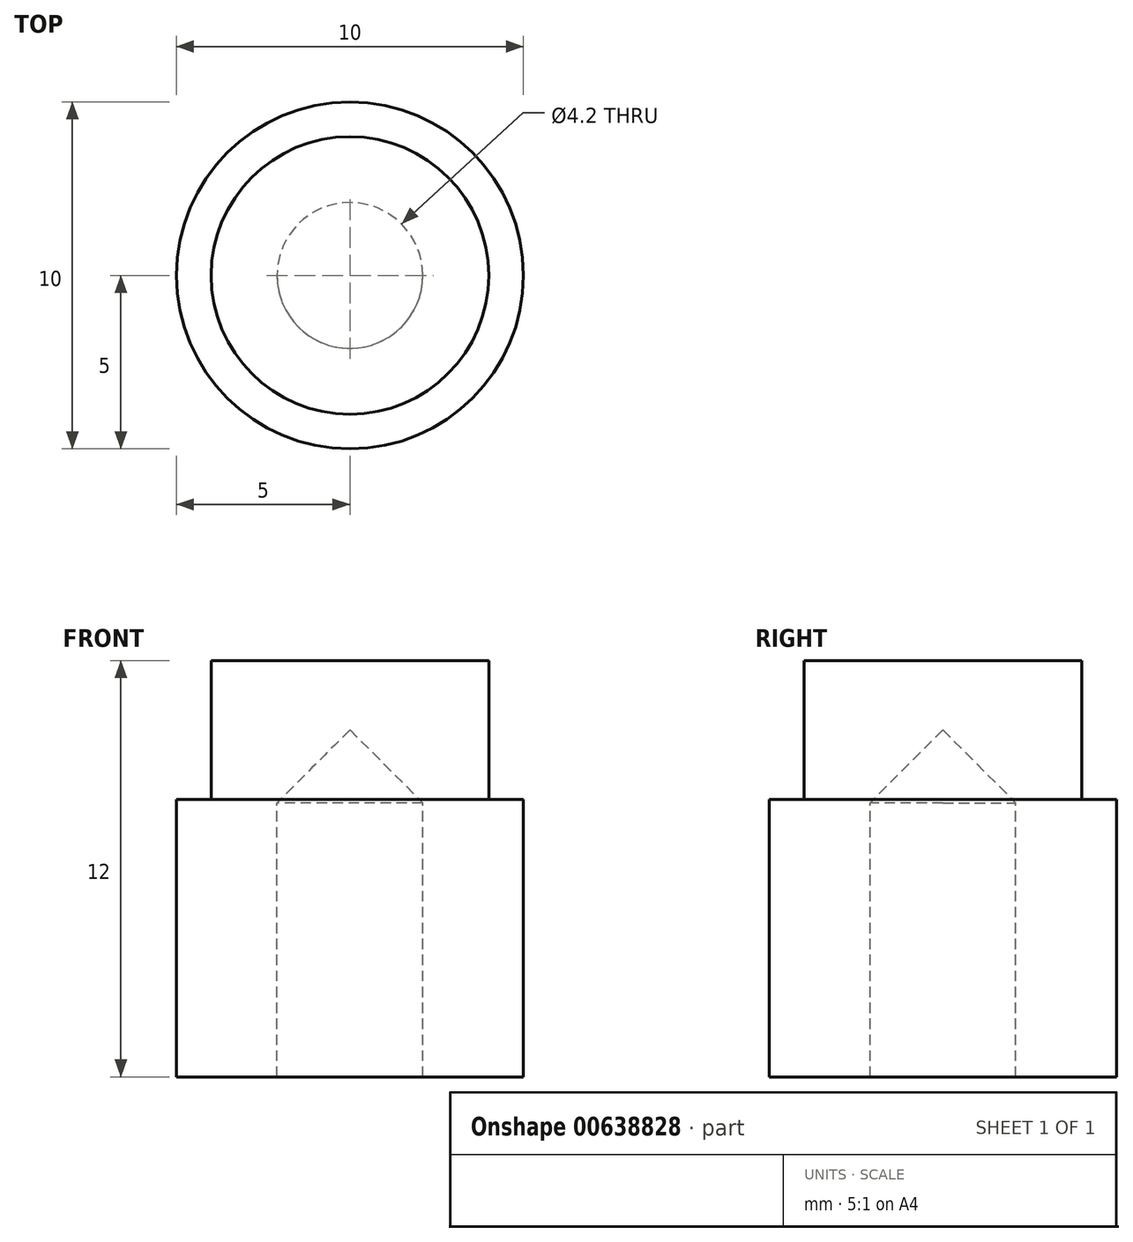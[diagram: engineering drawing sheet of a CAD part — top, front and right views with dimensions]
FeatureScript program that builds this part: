
annotation { "Feature Type Name" : "Feature", "Feature Type Description" : "" }
export const myFeature = defineFeature(function(context is Context, id is Id, definition is map)
    precondition{}
    {
        {
            var Q0;
            Q0=qCreatedBy(makeId("Top.planeOp"),FACE);
            var sketch = newSketch(context, id + "F0", { "sketchPlane" : qUnion([Q0])});
            skCircle(sketch, "E0", {"center": v(0, 0) * mm, "radius": 5 * mm});
            skCircle(sketch, "E1", {"center": v(0, 0) * mm, "radius": 4 * mm});
            skSolve(sketch);
        }
        {
            var Q0;
            Q0=makeQuery(id+"F0.imprint","IMPRINT",FACE,{"disambiguationData":[TD([[makeQuery(id+"F0.imprint","IMPRINT",EDGE,{"derivedFrom":sQuery(id+"F0.wireOp",EDGE,"E0")}),1.0]])]});
            extrude(context, id + "F1", {"entities" : qUnion([Q0]), "depth" : 8 * mm, "offsetDistance" : 25 * mm});
        }
        {
            var Q0;
            Q0=makeQuery(id+"F0.imprint","IMPRINT",FACE,{"disambiguationData":[TD([[makeQuery(id+"F0.imprint","IMPRINT",EDGE,{"derivedFrom":sQuery(id+"F0.wireOp",EDGE,"E1")}),1.0]])]});
            extrude(context, id + "F2", {"entities" : qUnion([Q0]), "operationType" : NewBodyOperationType.ADD, "depth" : 12 * mm, "offsetDistance" : 25 * mm});
        }
        {
            var Q0;
            Q0=qCreatedBy(makeId("Front.planeOp"),FACE);
            var sketch = newSketch(context, id + "F3", { "sketchPlane" : qUnion([Q0])});
            skLineSegment(sketch, "E2", {"start": v(2.1, 0) * mm, "end": v(2.1, 7.9) * mm});
            skLineSegment(sketch, "E3", {"start": v(2.1, 7.9) * mm, "end": v(0, 10) * mm});
            skLineSegment(sketch, "E4", {"start": v(0, 0) * mm, "end": v(0, 10) * mm, "construction": true});
            skLineSegment(sketch, "E5", {"start": v(2.1, 0) * mm, "end": v(2.1, -3.65) * mm});
            skLineSegment(sketch, "E6", {"start": v(2.1, -3.65) * mm, "end": v(0, -3.65) * mm});
            skLineSegment(sketch, "E7", {"start": v(0, -3.65) * mm, "end": v(0, 10) * mm});
            skSolve(sketch);
        }
        {
            var Q0;
            Q0=makeQuery(id+"F3.imprint","IMPRINT",FACE,{"disambiguationData":[TD([[makeQuery(id+"F3.imprint","IMPRINT",EDGE,{"derivedFrom":sQuery(id+"F3.wireOp",EDGE,"E2")}),1.0]])]});
            var Q1;
            Q1=sQuery(id+"F3.wireOp",EDGE,"E7");
            revolve(context, id + "F4", {"operationType" : NewBodyOperationType.REMOVE, "entities" : qUnion([Q0]), "axis" : qUnion([Q1]), "revolveType" : RevolveType.FULL, "oppositeDirection" : true});
        }
    });
